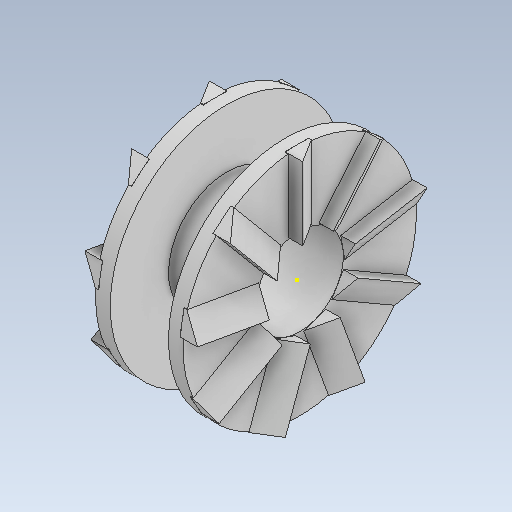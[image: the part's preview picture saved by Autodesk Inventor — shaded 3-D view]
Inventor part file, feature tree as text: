
AUTODESK INVENTOR PART (.ipt)
format: ipt  version: 2021 (Build 250183000, 183)  size: 367,616 bytes
history: native  units: in
note: dims shown in document units (in); Inventor stores cm internally (conversion verified against a paired STEP export)
features: sketch x10, pattern_circular x4, plane x2, loft x2, extrude x2, revolve x1
ambient origin geometry x8: Origin, YZ Plane, XZ Plane, XY Plane, X Axis, Y Axis, Z Axis, Center Point
bodies: Solid1 (feature_tree)
feature tree (21):
  revolve  "Revolution1"  [1 undecoded]
  sketch  "Sketch3"  dims[d2=0.1575in d3=0.7874in d4=3.1496in]
  sketch  "Sketch5"  dims[d5=3.1496in d6=1.5748in]
  sketch  "Sketch6"  dims[d7=90.0deg d16=1.1811in]
  plane  "Work Plane1"
  plane  "Work Plane2"
  loft  "Loft1"
  pattern_circular  "Circular Pattern1"  Count=8  [1 undecoded]
  extrude  "Extrusion2"  Depth=1.5748in
  pattern_circular  "Circular Pattern2"  Count=3  [1 undecoded]
  loft  "Loft2"
  pattern_circular  "Circular Pattern3"  Angle=90.0deg  [1 undecoded]
  extrude  "Extrusion3"  TaperAngle=0.0deg  [1 undecoded]
  pattern_circular  "Circular Pattern4"  Count=9 Angle=360.0deg
  sketch  "Sketch1"  dims[d0=0.7874in d1=0.1575in]
  sketch  "Sketch7"  dims[d28=0.2362in d29=0.9843in]
  sketch  "Sketch8"  dims[d30=-0.1575in d31=0.1575in]
  sketch  "Sketch9"  dims[d32=0.9843in]
  sketch  "Sketch11"  dims[d33=0.2362in]
  sketch  "Sketch12"  dims[d34=0.0394in]
  sketch  "Sketch13"  dims[d35=0.9843in d36=0.0in d37=90.0deg d38=0.0in d39=90.0deg d40=3.5433in d41=360.0deg d43=0.0394in d44=0.0in d45=3.5433in d46=360.0deg d53=0.2362in d54=0.9843in d55=0.0394in d56=0.9843in d57=0.0in d58=90.0deg d59=0.0in d60=90.0deg d61=3.5433in d62=360.0deg d64=0.0394in d65=0.0in d66=3.5433in d67=360.0deg]
note: 5 required parameter values undecoded (feature->parameter linkage not recoverable at this tier; creation-order binding heuristic only, values carry confidence <= 0.55)